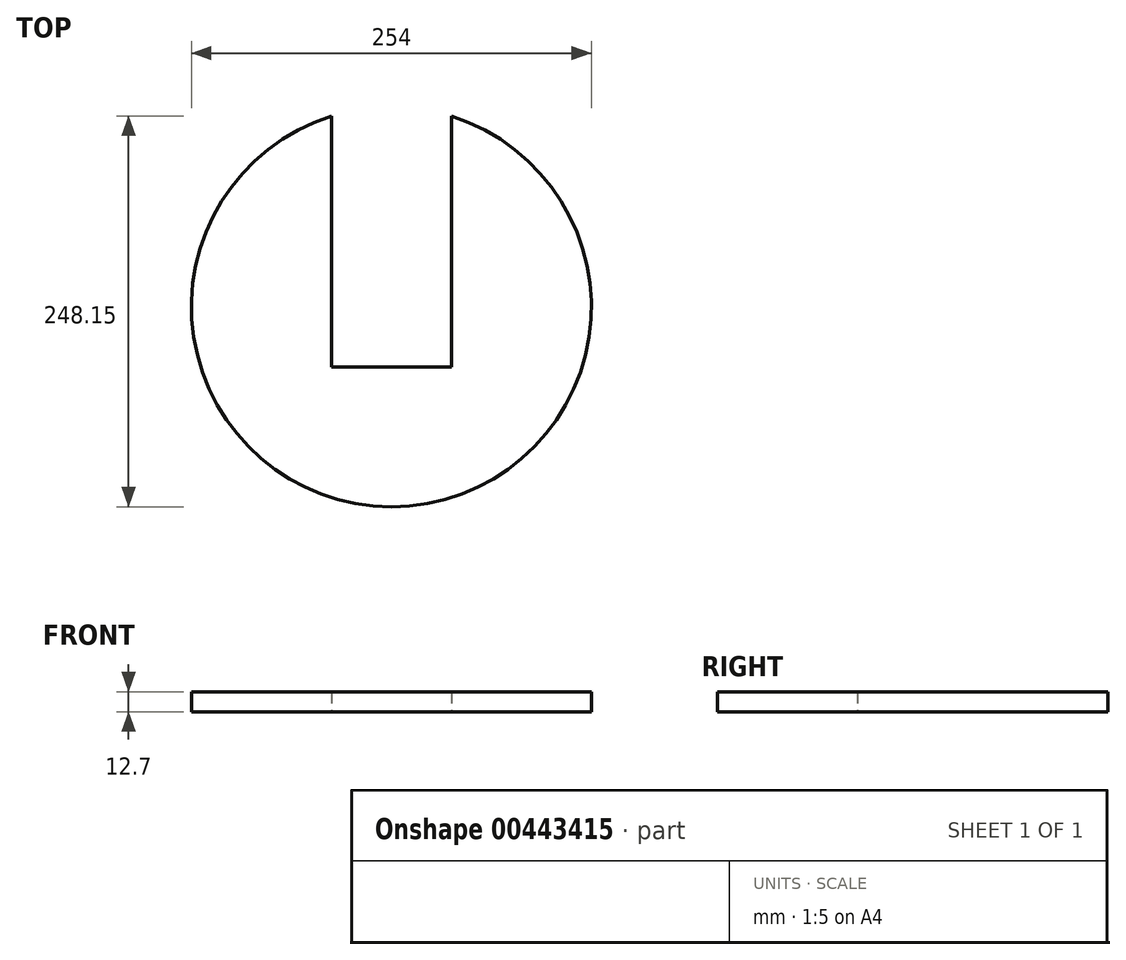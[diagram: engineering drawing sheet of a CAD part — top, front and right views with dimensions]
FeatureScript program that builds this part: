
annotation { "Feature Type Name" : "Feature", "Feature Type Description" : "" }
export const myFeature = defineFeature(function(context is Context, id is Id, definition is map)
    precondition{}
    {
        {
            var Q0;
            Q0=qCreatedBy(makeId("Top.planeOp"),FACE);
            var sketch = newSketch(context, id + "F0", { "sketchPlane" : qUnion([Q0])});
            skArc(sketch, "E0", {"start": v(-38.1, 121.15) * mm, "mid": v(0, -127) * mm, "end": v(38.1, 121.15) * mm});
            skLineSegment(sketch, "E1.top", {"start": v(38.1, -38.1) * mm, "end": v(-38.1, -38.1) * mm});
            skLineSegment(sketch, "E1.left", {"start": v(38.1, 121.15) * mm, "end": v(38.1, -38.1) * mm});
            skLineSegment(sketch, "E1.right", {"start": v(-38.1, 121.15) * mm, "end": v(-38.1, -38.1) * mm});
            skPoint(sketch, "E1.middle", {"position": v(0, 41.52) * mm});
            skSolve(sketch);
        }
        {
            var Q0;
            Q0 = qSketchRegion(id + "F0", true);
            extrude(context, id + "F1", {"entities" : qUnion([Q0]), "depth" : 12.7 * mm});
        }
    });
